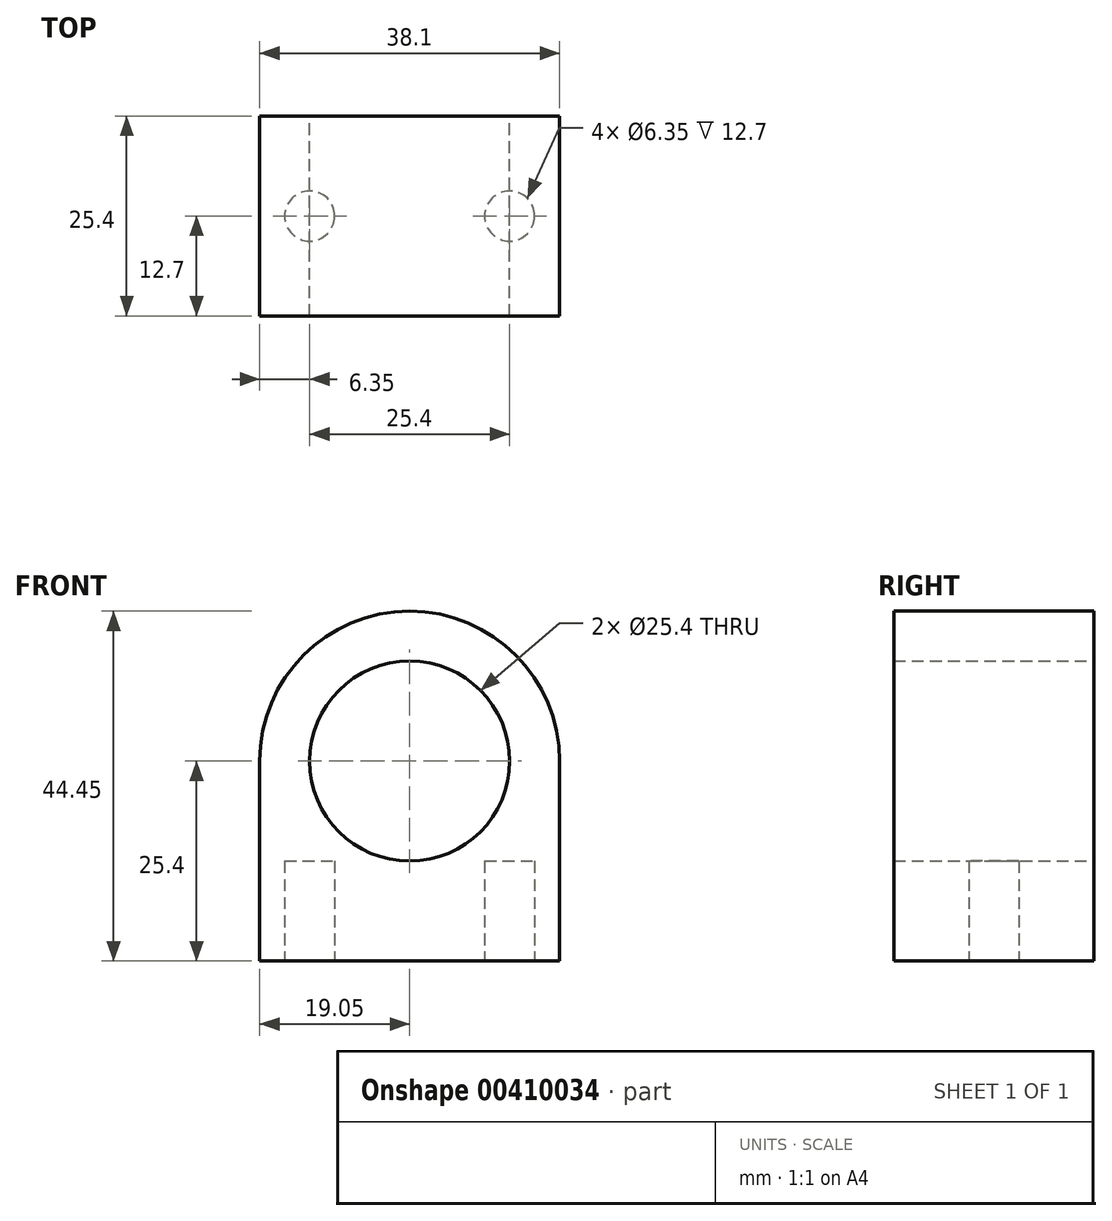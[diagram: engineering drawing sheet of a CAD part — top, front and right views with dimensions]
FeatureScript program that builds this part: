
annotation { "Feature Type Name" : "Feature", "Feature Type Description" : "" }
export const myFeature = defineFeature(function(context is Context, id is Id, definition is map)
    precondition{}
    {
        {
            var Q0;
            Q0=qCreatedBy(makeId("Front.planeOp"),FACE);
            var sketch = newSketch(context, id + "F0", { "sketchPlane" : qUnion([Q0])});
            skLineSegment(sketch, "E0", {"start": v(-27.73, 0) * mm, "end": v(32.6, 0) * mm, "construction": true});
            skLineSegment(sketch, "E1", {"start": v(0, 25.4) * mm, "end": v(0, -62.02) * mm, "construction": true});
            skCircle(sketch, "E2", {"center": v(0, 0) * mm, "radius": 12.7 * mm});
            skArc(sketch, "E3", {"start": v(19.05, 0) * mm, "mid": v(0, 19.05) * mm, "end": v(-19.05, 0) * mm});
            skLineSegment(sketch, "E4", {"start": v(-19.05, 0) * mm, "end": v(-19.05, -25.4) * mm});
            skLineSegment(sketch, "E5", {"start": v(-19.05, -25.4) * mm, "end": v(0, -25.4) * mm});
            skLineSegment(sketch, "E6.MirrorCS", {"start": v(19.05, -25.4) * mm, "end": v(0, -25.4) * mm});
            skLineSegment(sketch, "E7.MirrorCS", {"start": v(19.05, 0) * mm, "end": v(19.05, -25.4) * mm});
            skSolve(sketch);
        }
        {
            var Q0;
            Q0 = qSketchRegion(id + "F0", true);
            extrude(context, id + "F1", {"entities" : qUnion([Q0]), "endBound" : BoundingType.SYMMETRIC, "depth" : 25.4 * mm});
        }
        {
            var Q0;
            Q0=makeQuery(id+"F1.opExtrude","SWEPT_FACE",FACE,{"disambiguationData":[OSD([sQuery(id+"F0.wireOp",EDGE,"E5"),sQuery(id+"F0.wireOp",EDGE,"E6.MirrorCS")])]});
            var sketch = newSketch(context, id + "F2", { "sketchPlane" : qUnion([Q0])});
            skLineSegment(sketch, "E8", {"start": v(-33.9, 0) * mm, "end": v(42.55, 0) * mm, "construction": true});
            skCircle(sketch, "E9", {"center": v(-12.7, 0) * mm, "radius": 3.17 * mm});
            skLineSegment(sketch, "E10", {"start": v(0, 19.72) * mm, "end": v(0, -27.33) * mm, "construction": true});
            skCircle(sketch, "E11.MirrorC", {"center": v(12.7, 0) * mm, "radius": 3.17 * mm});
            skSolve(sketch);
        }
        {
            var Q0;
            Q0 = qSketchRegion(id + "F2", true);
            extrude(context, id + "F3", {"entities" : qUnion([Q0]), "operationType" : NewBodyOperationType.REMOVE, "oppositeDirection" : true, "depth" : 12.7 * mm});
        }
    });
